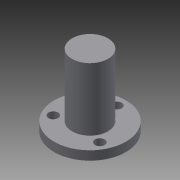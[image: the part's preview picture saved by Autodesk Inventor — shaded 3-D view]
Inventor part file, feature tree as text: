
AUTODESK INVENTOR PART (.ipt)
format: ipt  version: 2013 (Build 170138000, 138)  size: 91,136 bytes
history: native  units: mm
features: extrude x3, sketch x3, pattern_circular x1
ambient origin geometry x8: Origin, YZ Plane, XZ Plane, XY Plane, X Axis, Y Axis, Z Axis, Center Point
bodies: Solid1 (feature_tree)
feature tree (7):
  extrude  "Extrusion1"  Depth=4.7752mm TaperAngle=0.0deg
  extrude  "Extrusion2"  Depth=38.1mm TaperAngle=0.0deg
  extrude  "Extrusion3"  Depth=14.2875mm
  pattern_circular  "Circular Pattern1"  [2 undecoded]
  sketch  "Sketch1"  dims[d0=38.1mm d3=4.7752mm d4=0.0mm]
  sketch  "Sketch2"  dims[d5=19.05mm d8=38.1mm d9=0.0mm]
  sketch  "Sketch3"  dims[d10=5.1562mm d12=14.2875mm d13=38.1mm d14=0.0mm d15=30.0mm d16=360.0deg]
note: 2 required parameter values undecoded (feature->parameter linkage not recoverable at this tier; creation-order binding heuristic only, values carry confidence <= 0.55)
